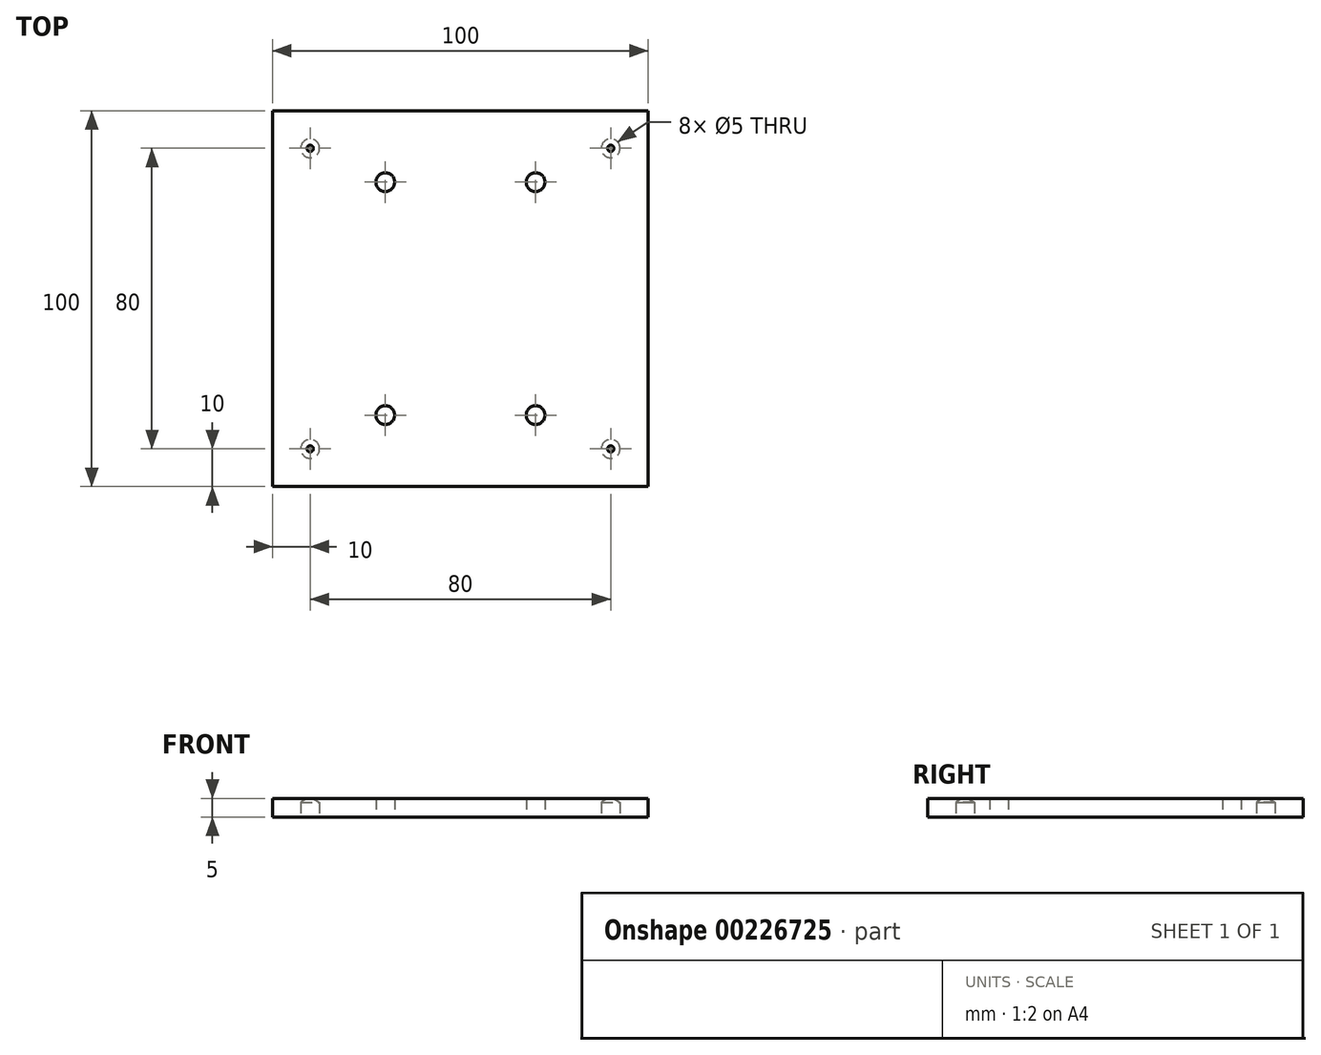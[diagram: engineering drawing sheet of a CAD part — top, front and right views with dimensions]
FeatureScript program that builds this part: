
annotation { "Feature Type Name" : "Feature", "Feature Type Description" : "" }
export const myFeature = defineFeature(function(context is Context, id is Id, definition is map)
    precondition{}
    {
        {
            var Q0;
            Q0=qCreatedBy(makeId("Top.planeOp"),FACE);
            var sketch = newSketch(context, id + "F0", { "sketchPlane" : qUnion([Q0])});
            skLineSegment(sketch, "E0.bottom", {"start": v(0, 0) * mm, "end": v(80, 0) * mm});
            skLineSegment(sketch, "E0.top", {"start": v(0, -80) * mm, "end": v(80, -80) * mm});
            skLineSegment(sketch, "E0.left", {"start": v(0, 0) * mm, "end": v(0, -80) * mm});
            skLineSegment(sketch, "E0.right", {"start": v(80, 0) * mm, "end": v(80, -80) * mm});
            skPoint(sketch, "E1.0", {"position": v(80, 0) * mm});
            skLineSegment(sketch, "E2.0", {"start": v(-10, 10) * mm, "end": v(90, 10) * mm});
            skLineSegment(sketch, "E2.1", {"start": v(-10, 10) * mm, "end": v(-10, -90) * mm});
            skLineSegment(sketch, "E2.2", {"start": v(-10, -90) * mm, "end": v(90, -90) * mm});
            skLineSegment(sketch, "E2.3", {"start": v(90, 10) * mm, "end": v(90, -90) * mm});
            skSolve(sketch);
        }
        {
            var Q0;
            Q0=makeQuery(id+"F0.imprint","IMPRINT",FACE,{"disambiguationData":[TD([[makeQuery(id+"F0.imprint","IMPRINT",EDGE,{"derivedFrom":sQuery(id+"F0.wireOp",EDGE,"E0.bottom")}),-1.0]])]});
            var Q1;
            Q1=makeQuery(id+"F0.imprint","IMPRINT",FACE,{"disambiguationData":[TD([[makeQuery(id+"F0.imprint","IMPRINT",EDGE,{"derivedFrom":sQuery(id+"F0.wireOp",EDGE,"E0.bottom")}),1.0]])]});
            extrude(context, id + "F1", {"entities" : qUnion([Q0, Q1]), "depth" : 5 * mm});
        }
        {
            var Q0;
            Q0=qCreatedBy(makeId("Top.planeOp"),FACE);
            var sketch = newSketch(context, id + "F2", { "sketchPlane" : qUnion([Q0])});
            skLineSegment(sketch, "E3.bottom", {"start": v(20, -9) * mm, "end": v(60, -9) * mm, "construction": true});
            skLineSegment(sketch, "E3.top", {"start": v(20, -71) * mm, "end": v(60, -71) * mm, "construction": true});
            skLineSegment(sketch, "E3.left", {"start": v(20, -9) * mm, "end": v(20, -71) * mm, "construction": true});
            skLineSegment(sketch, "E3.right", {"start": v(60, -9) * mm, "end": v(60, -71) * mm, "construction": true});
            skPoint(sketch, "E3.middle", {"position": v(40, -40) * mm});
            skCircle(sketch, "E4", {"center": v(20, -71) * mm, "radius": 2.5 * mm});
            skCircle(sketch, "E5", {"center": v(60, -71) * mm, "radius": 2.5 * mm});
            skCircle(sketch, "E6", {"center": v(20, -9) * mm, "radius": 2.5 * mm});
            skCircle(sketch, "E7", {"center": v(60, -9) * mm, "radius": 2.5 * mm});
            skSolve(sketch);
        }
        {
            var Q0;
            Q0=sQuery(id+"F2.wireOp",VERTEX,"E3.bottom.start");
            var Q1;
            Q1=sQuery(id+"F2.wireOp",VERTEX,"E7.center");
            var Q2;
            Q2=sQuery(id+"F2.wireOp",VERTEX,"E5.center");
            var Q3;
            Q3=sQuery(id+"F2.wireOp",VERTEX,"E4.center");
            var Q4;
            Q4=makeQuery(id+"F1.opExtrude","SWEPT_BODY",BODY,{"disambiguationData":[OSD([sQuery(id+"F0.wireOp",EDGE,"E2.0"),sQuery(id+"F0.wireOp",EDGE,"E2.1"),sQuery(id+"F0.wireOp",EDGE,"E2.2"),sQuery(id+"F0.wireOp",EDGE,"E2.3")])]});
            hole(context, id + "F3", {"style" : HoleStyle.SIMPLE, "endStyle" : HoleEndStyle.THROUGH, "oppositeDirection" : true, "holeDiameter" : 5 * mm, "locations" : qUnion([Q0, Q1, Q2, Q3]), "scope" : qUnion([Q4]), "isTappedThrough" : true});
        }
        {
            var Q0;
            Q0=sQuery(id+"F0.wireOp",VERTEX,"E0.left.end");
            var Q1;
            Q1=sQuery(id+"F0.wireOp",VERTEX,"E0.right.end");
            var Q2;
            Q2=sQuery(id+"F0.wireOp",VERTEX,"E1.0");
            var Q3;
            Q3=sQuery(id+"F0.wireOp",VERTEX,"E0.bottom.start");
            var Q4;
            Q4=makeQuery(id+"F1.opExtrude","SWEPT_BODY",BODY,{"disambiguationData":[OSD([sQuery(id+"F0.wireOp",EDGE,"E2.0"),sQuery(id+"F0.wireOp",EDGE,"E2.1"),sQuery(id+"F0.wireOp",EDGE,"E2.2"),sQuery(id+"F0.wireOp",EDGE,"E2.3")])]});
            hole(context, id + "F4", {"style" : HoleStyle.SIMPLE, "endStyle" : HoleEndStyle.BLIND, "oppositeDirection" : true, "holeDiameter" : 5 * mm, "holeDepth" : 4 * mm, "locations" : qUnion([Q0, Q1, Q2, Q3]), "scope" : qUnion([Q4])});
        }
    });
